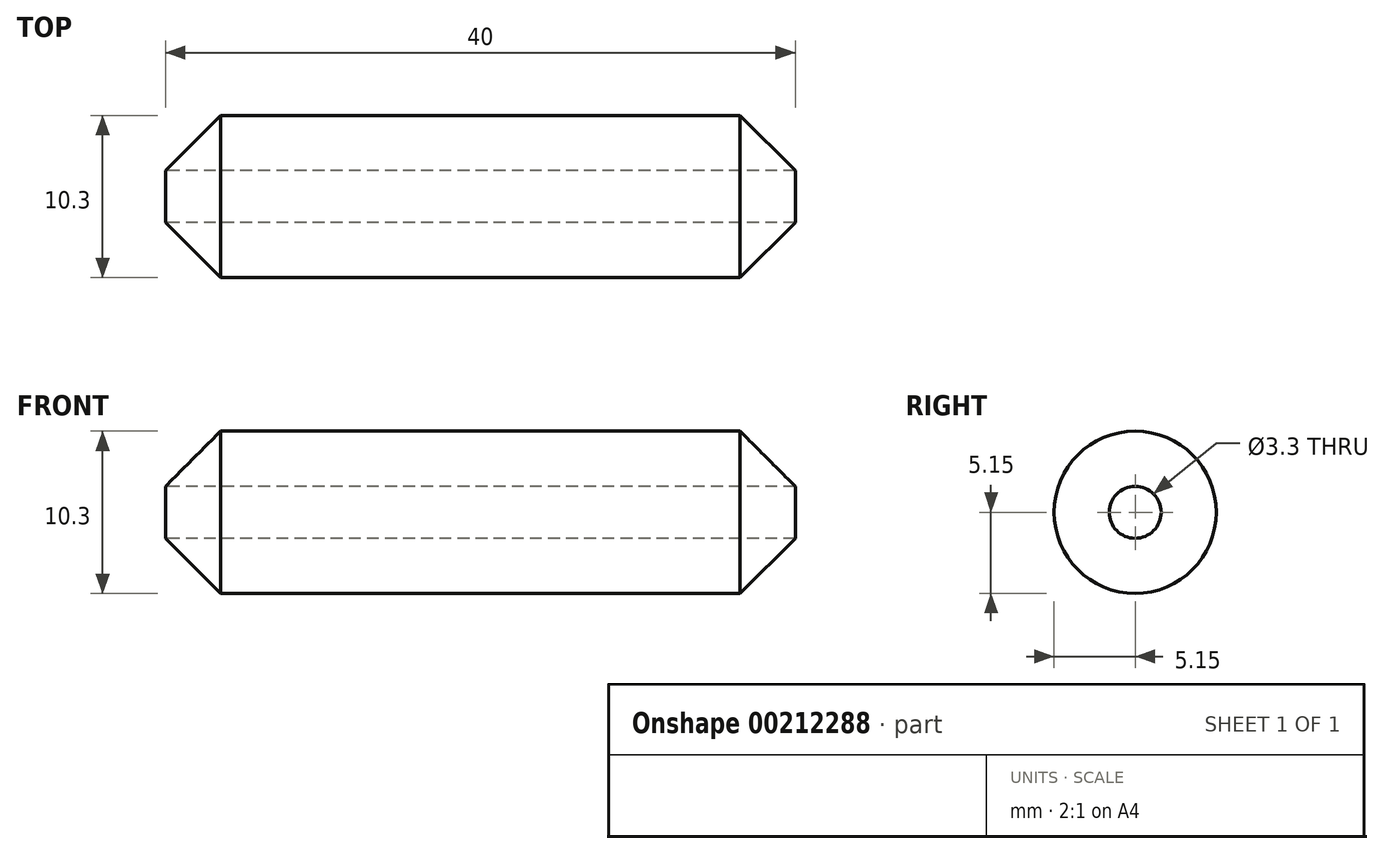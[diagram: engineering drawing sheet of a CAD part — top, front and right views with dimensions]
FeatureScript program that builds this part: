
annotation { "Feature Type Name" : "Feature", "Feature Type Description" : "" }
export const myFeature = defineFeature(function(context is Context, id is Id, definition is map)
    precondition{}
    {
        {
            var Q0;
            Q0=qCreatedBy(makeId("Front.planeOp"),FACE);
            var sketch = newSketch(context, id + "F0", { "sketchPlane" : qUnion([Q0])});
            skLineSegment(sketch, "E0.bottom", {"start": v(0, 0) * mm, "end": v(40, 0) * mm});
            skLineSegment(sketch, "E0.top", {"start": v(0, 3.5) * mm, "end": v(40, 3.5) * mm});
            skLineSegment(sketch, "E0.left", {"start": v(0, 0) * mm, "end": v(0, 3.5) * mm});
            skLineSegment(sketch, "E0.right", {"start": v(40, 0) * mm, "end": v(40, 3.5) * mm});
            skLineSegment(sketch, "E1", {"start": v(0, 0) * mm, "end": v(3.5, 3.5) * mm});
            skPoint(sketch, "E2", {"position": v(40, 0) * mm});
            skPoint(sketch, "E3", {"position": v(3.5, 3.5) * mm});
            skLineSegment(sketch, "E4", {"start": v(40, 0) * mm, "end": v(36.5, 3.5) * mm});
            skLineSegment(sketch, "E5", {"start": v(36.5, 3.5) * mm, "end": v(36.5, 0) * mm});
            skPoint(sketch, "E6", {"position": v(36.5, 3.5) * mm});
            skPoint(sketch, "E7", {"position": v(36.5, 0) * mm});
            skLineSegment(sketch, "E8", {"start": v(3.5, 3.5) * mm, "end": v(3.5, 0) * mm});
            skLineSegment(sketch, "E9", {"start": v(0, -1.65) * mm, "end": v(40, -1.65) * mm});
            skLineSegment(sketch, "E10", {"start": v(36.5, 3.5) * mm, "end": v(36.5, 13.5) * mm});
            skLineSegment(sketch, "E11", {"start": v(36.5, 0) * mm, "end": v(36.5, -10) * mm});
            skPoint(sketch, "E12", {"position": v(36.5, 13.5) * mm});
            skPoint(sketch, "E13", {"position": v(36.5, -10) * mm});
            skPoint(sketch, "E14", {"position": v(36.5, -5) * mm});
            skPoint(sketch, "E15", {"position": v(36.5, 8.5) * mm});
            skSolve(sketch);
        }
        {
            var Q0;
            {var subQ0=sQuery(id+"F0.wireOp",EDGE,"E1");Q0=makeQuery(id+"F0.imprint","IMPRINT",FACE,{"disambiguationData":[TD([[makeQuery(id+"F0.imprint","IMPRINT",EDGE,{"derivedFrom":subQ0}),-1.0]])]});}
            var Q1;
            {var subQ0=sQuery(id+"F0.wireOp",EDGE,"E5");Q1=makeQuery(id+"F0.imprint","IMPRINT",FACE,{"disambiguationData":[TD([[makeQuery(id+"F0.imprint","IMPRINT",EDGE,{"derivedFrom":subQ0}),-1.0]])]});}
            var Q2;
            {var subQ0=sQuery(id+"F0.wireOp",EDGE,"E4");Q2=makeQuery(id+"F0.imprint","IMPRINT",FACE,{"disambiguationData":[TD([[makeQuery(id+"F0.imprint","IMPRINT",EDGE,{"derivedFrom":subQ0}),1.0]])]});}
            var Q3;
            Q3=sQuery(id+"F0.wireOp",EDGE,"E9");
            revolve(context, id + "F1", {"entities" : qUnion([Q0, Q1, Q2]), "axis" : qUnion([Q3]), "revolveType" : RevolveType.FULL});
        }
    });
